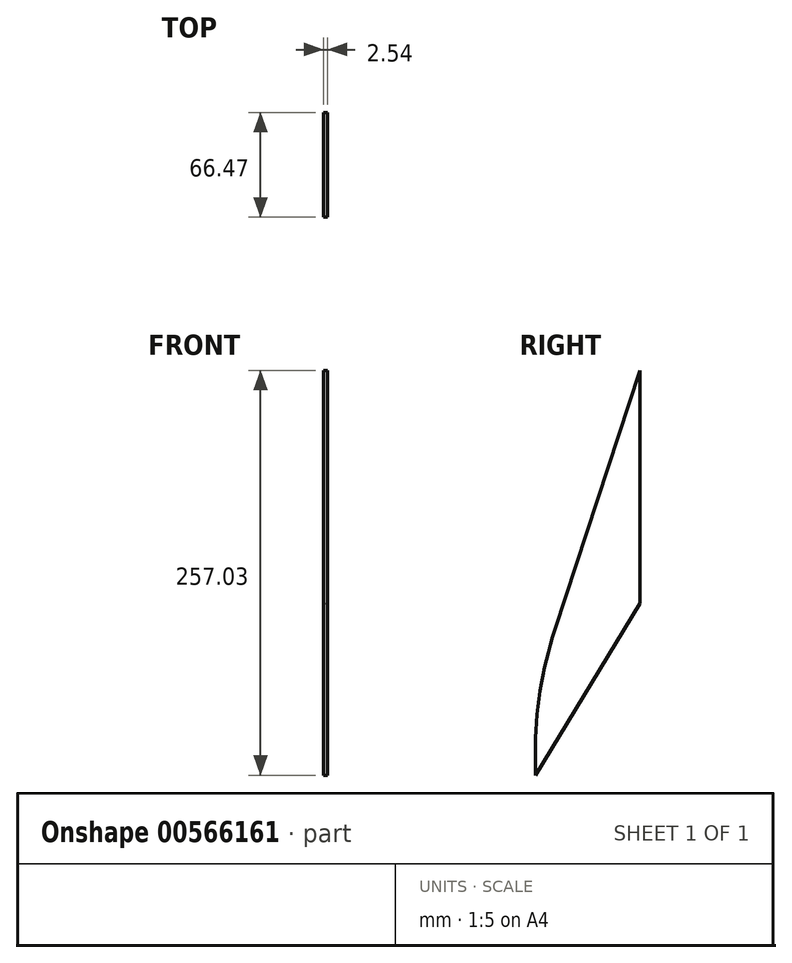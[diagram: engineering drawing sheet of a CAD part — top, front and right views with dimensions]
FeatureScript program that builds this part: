
annotation { "Feature Type Name" : "Feature", "Feature Type Description" : "" }
export const myFeature = defineFeature(function(context is Context, id is Id, definition is map)
    precondition{}
    {
        {
            var Q0;
            Q0=qCreatedBy(makeId("Right.planeOp"),FACE);
            var sketch = newSketch(context, id + "F0", { "sketchPlane" : qUnion([Q0])});
            skLineSegment(sketch, "E0", {"start": v(-98.43, 0) * mm, "end": v(-98.43, 152.4) * mm});
            skLineSegment(sketch, "E1", {"start": v(-98.42, 152.4) * mm, "end": v(-155.45, -21.75) * mm});
            skLineSegment(sketch, "E2", {"start": v(-168.06, -100.8) * mm, "end": v(-168.06, -114.3) * mm});
            skLineSegment(sketch, "E3", {"start": v(-168.06, -114.3) * mm, "end": v(-98.42, 0) * mm});
            skPoint(sketch, "E4.visualSharp", {"position": v(-168.06, -60.27) * mm});
            skArc(sketch, "E4.filletArc", {"start": v(-155.45, -21.75) * mm, "mid": v(-164.88, -60.77) * mm, "end": v(-168.06, -100.8) * mm});
            skSolve(sketch);
        }
        {
            var Q0;
            Q0 = qSketchRegion(id + "F0", true);
            extrude(context, id + "F1", {"entities" : qUnion([Q0]), "endBound" : BoundingType.SYMMETRIC, "depth" : 2.54 * mm, "offsetDistance" : 25.4 * mm});
        }
        {
            var Q0;
            Q0=qCreatedBy(makeId("Top.planeOp"),FACE);
            var sketch = newSketch(context, id + "F2", { "sketchPlane" : qUnion([Q0])});
            skCircle(sketch, "E5", {"center": v(0, 0) * mm, "radius": 101.6 * mm});
            skSolve(sketch);
        }
        {
            var Q0;
            Q0 = qSketchRegion(id + "F2", true);
            extrude(context, id + "F3", {"entities" : qUnion([Q0]), "operationType" : NewBodyOperationType.REMOVE, "endBound" : BoundingType.SYMMETRIC, "depth" : 334.26 * mm, "offsetDistance" : 25.4 * mm});
        }
    });
